# Revit family: MECON mag-flux T4 compact threaded_PTFE
name_source: partatom
category: Rohrzubehör
units: mm (PartAtom-declared; Revit-internal decimal feet)

## family parameters
Arbeitsebenenbasiert = Nein
Beim Laden mit Abzugskörper schneiden = Nein
Bemaßung runder Anschluss = Radius verwenden
Gemeinsam genutzt = Nein
Immer vertikal = Ja
OmniClass-Nummer = 23.60.10.17
OmniClass-Titel = Flow Meters
Teiletyp = Ventil - Zerlegung in

## types (6) — shared parameters
Approval = VdS
Black = Metal - black
Build in Length = 150 mm  [stored 0.492126 ft]
Dark Grey = Metal - RAL7024
Delivery Time = app. 3 weeks
Download Test Certificate = https://download.mecon.de
Glass = Glass-
Grey = Metal - grey
Hersteller = MECON GmbH, Röntgenstraße 105, 50169 Kerpen, Germany
IfcExportAs = IfcFlowMeter
IfcExportType = FLOWMETER
Operating Manual = https://www.mecon.de
URL = https://www.mecon.de
VdS Approval = https://www.mecon.de
Website Product = https://www.mecon.de
iB = 80 mm  [stored 0.262467 ft]
iFM = Nein
iLPCB = Nein
iVdS = Ja
zero-valued in all types: Vorgabe-Ansicht

## per-type parameters (varying)
| type | Flow Range | Modell | Nominal_Diameter | Nominal_Radius | Order Code | iD1 | iD2 | iH | iR1 |
| G 1/2", 0-106 l/min, 0-28 USgpm | 0 - 106 l/min / 0 - 28 USgpm | Threaded connection G 1/2, lining: PTFE, electrodes: stainless steel, remote, 230 V AC, 50/60 Hz, 4 - 20 mA, with transducer | 13 mm | 6 mm | T4-P-G015-1-11BB4L | 130 mm | 115 mm  [stored 0.377297 ft] | 53 mm | 10.35 mm  [stored 0.0339567 ft] |
| G 2", 0-1180 l/min, 0-310 USgpm | 0 - 1180 l/min / 0 - 310 USgpm | Threaded connection G 2, lining: PTFE, electrodes: stainless steel, remote, 230 V AC, 50/60 Hz, 4 - 20 mA, with transducer | 51 mm | 25 mm | T4-P-G050-1-11BB4L | 140 mm  [stored 0.459318 ft] | 120 mm  [stored 0.393701 ft] | 57 mm  [stored 0.187008 ft] | 29.4 mm  [stored 0.0964567 ft] |
| G 1 1/2", 0-750 l/min, 0-200 USgpm | 0 - 750 l/min / 0 - 200 USgpm | Threaded connection G 1 1/2, lining: PTFE, electrodes: stainless steel, remote,  230 V AC, 50/60 Hz, 4 - 20 mA, with transducer | 38 mm | 19 mm | T4-P-G040-1-11BB4L | 130 mm | 115 mm  [stored 0.377297 ft] | 53 mm | 23.05 mm |
| G 1 1/4", 0-480 l/min, 0-128 USgpm | 0 - 480 l/min / 0 - 128 USgpm | Threaded connection G 1 1/4, lining: PTFE, electrodes: stainless steel,  remote,  230 V AC, 50/60 Hz, 4 - 20 mA, with transducer | 32 mm | 16 mm | T4-P-G032-1-11BB4L | 130 mm | 115 mm  [stored 0.377297 ft] | 53 mm | 19.9 mm |
| G 1", 0-295 l/min, 0-78 USgpm | 0 - 295 l/min / 0 - 78 USgpm | Threaded connection G 1, lining: PTFE, electrodes: stainless steel, remote, 230 V AC, 50/60 Hz, 4 - 20 mA, with transducer | 25 mm | 13 mm | T4-P-G025-1-11BB4L | 130 mm | 115 mm  [stored 0.377297 ft] | 53 mm | 16.7 mm |
| G 3/4", 0-188 l/min, 0-50 USgpm | 0 - 188 l/min / 0 - 50 USgpm | Threaded connection G 3/4, lining: PTFE, electrodes: stainless steel, remote, 230 V AC, 50/60 Hz, 4 - 20 mA, with transducer | 19 mm | 10 mm | T4-P-G020-1-11BB4L | 130 mm | 115 mm  [stored 0.377297 ft] | 53 mm | 13.55 mm |

note: column(s) folded — value = type name in every type: Typenkommentare

note: [stored X ft] marks values corroborated as IEEE doubles in the binary element streams (Revit-internal decimal feet)
